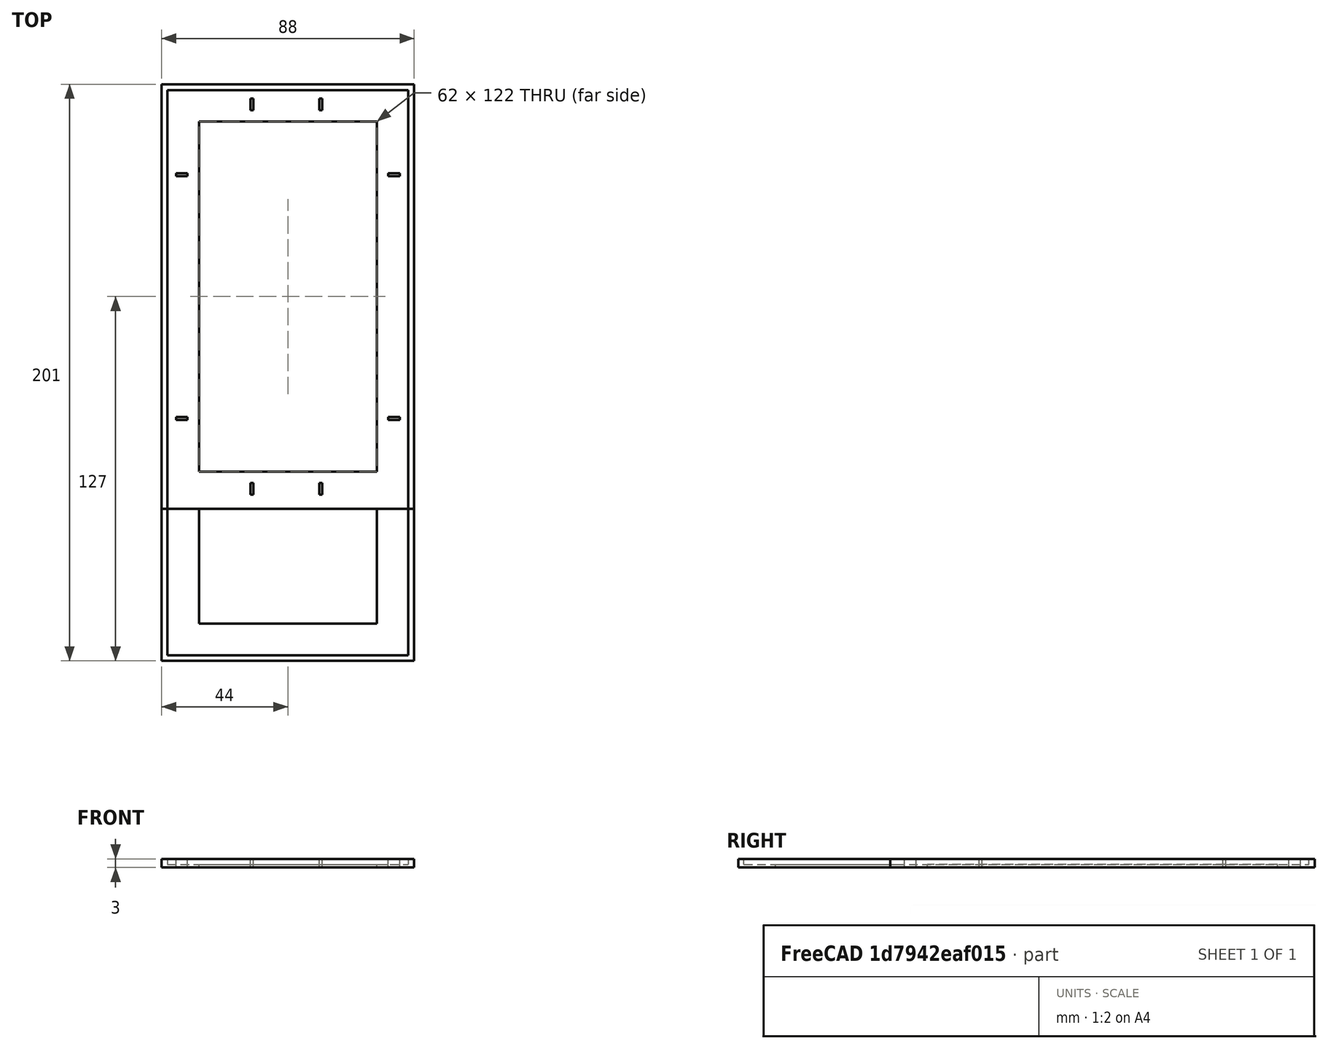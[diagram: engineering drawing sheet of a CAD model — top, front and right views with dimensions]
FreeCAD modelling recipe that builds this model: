
FCSTD DOCUMENT  (FreeCAD 0.16R)
Label: sonoff-T1-US-aufputz-und-Steckdose_v2.3_Adapter
License: All rights reserved
LicenseURL: http://en.wikipedia.org/wiki/All_rights_reserved
objects: Part::Box×14, Part::Cut×5
note: 19 computed .brp shape members not serialized (recipe doc carries the construction recipe); baked Part::Feature solids carry a one-line shape summary decoded from their .brp

FEATURE [Part::Box] Box  label="Cube"
  Height = 3
  Length = 88
  Width = 148
FEATURE [Part::Box] Box001  label="Cube001"
  Height = 3
  Length = 62
  Placement = pos=(13,13,0) rot=(0,0,1;0rad)
  Width = 122
FEATURE [Part::Cut] Cut
  Base = -> Box
  Tool = -> Box001
FEATURE [Part::Box] Box002  label="Cube002"
  Height = 2
  Length = 84
  Placement = pos=(2,2,1) rot=(0,0,1;0rad)
  Width = 144
FEATURE [Part::Cut] Cut001
  Base = -> Cut
  Tool = -> Box002
FEATURE [Part::Box] Box003  label="Cube003"
  Height = 3
  Length = 4
  Placement = pos=(5,31,0) rot=(0,0,1;0rad)
  Width = 1
FEATURE [Part::Box] Box004  label="Cube004"
  Height = 3
  Length = 4
  Placement = pos=(79,31,0) rot=(0,0,1;0rad)
  Width = 1
FEATURE [Part::Box] Box005  label="Cube005"
  Height = 3
  Length = 4
  Placement = pos=(5,116,0) rot=(0,0,1;0rad)
  Width = 1
FEATURE [Part::Box] Box006  label="Cube006"
  Height = 3
  Length = 4
  Placement = pos=(79,116,0) rot=(0,0,1;0rad)
  Width = 1
FEATURE [Part::Box] Box007  label="Cube007"
  Height = 3
  Length = 1
  Placement = pos=(31,5,0) rot=(0,0,1;0rad)
  Width = 4
FEATURE [Part::Box] Box008  label="Cube008"
  Height = 3
  Length = 1
  Placement = pos=(55,5,0) rot=(0,0,1;0rad)
  Width = 4
FEATURE [Part::Box] Box009  label="Cube009"
  Height = 3
  Length = 1
  Placement = pos=(31,139,0) rot=(0,0,1;0rad)
  Width = 4
FEATURE [Part::Box] Box010  label="Cube010"
  Height = 3
  Length = 1
  Placement = pos=(55,139,0) rot=(0,0,1;0rad)
  Width = 4
FEATURE [Part::Box] Box011  label="Cube011"
  Height = 3
  Length = 88
  Placement = pos=(0,-53,0) rot=(0,0,1;0rad)
  Width = 53
FEATURE [Part::Box] Box012  label="Cube012"
  Height = 2
  Length = 84
  Placement = pos=(2,-51,1) rot=(0,0,1;0rad)
  Width = 53
FEATURE [Part::Cut] Cut002
  Base = -> Box011
  Tool = -> Box012
FEATURE [Part::Cut] Cut003
  Base = -> Cut001
  Tool = -> Box012
FEATURE [Part::Box] Box013  label="Cube013"
  Height = 3
  Length = 62
  Placement = pos=(13,-40,0) rot=(0,0,1;0rad)
  Width = 40
FEATURE [Part::Cut] Cut004
  Base = -> Cut002
  Tool = -> Box013
